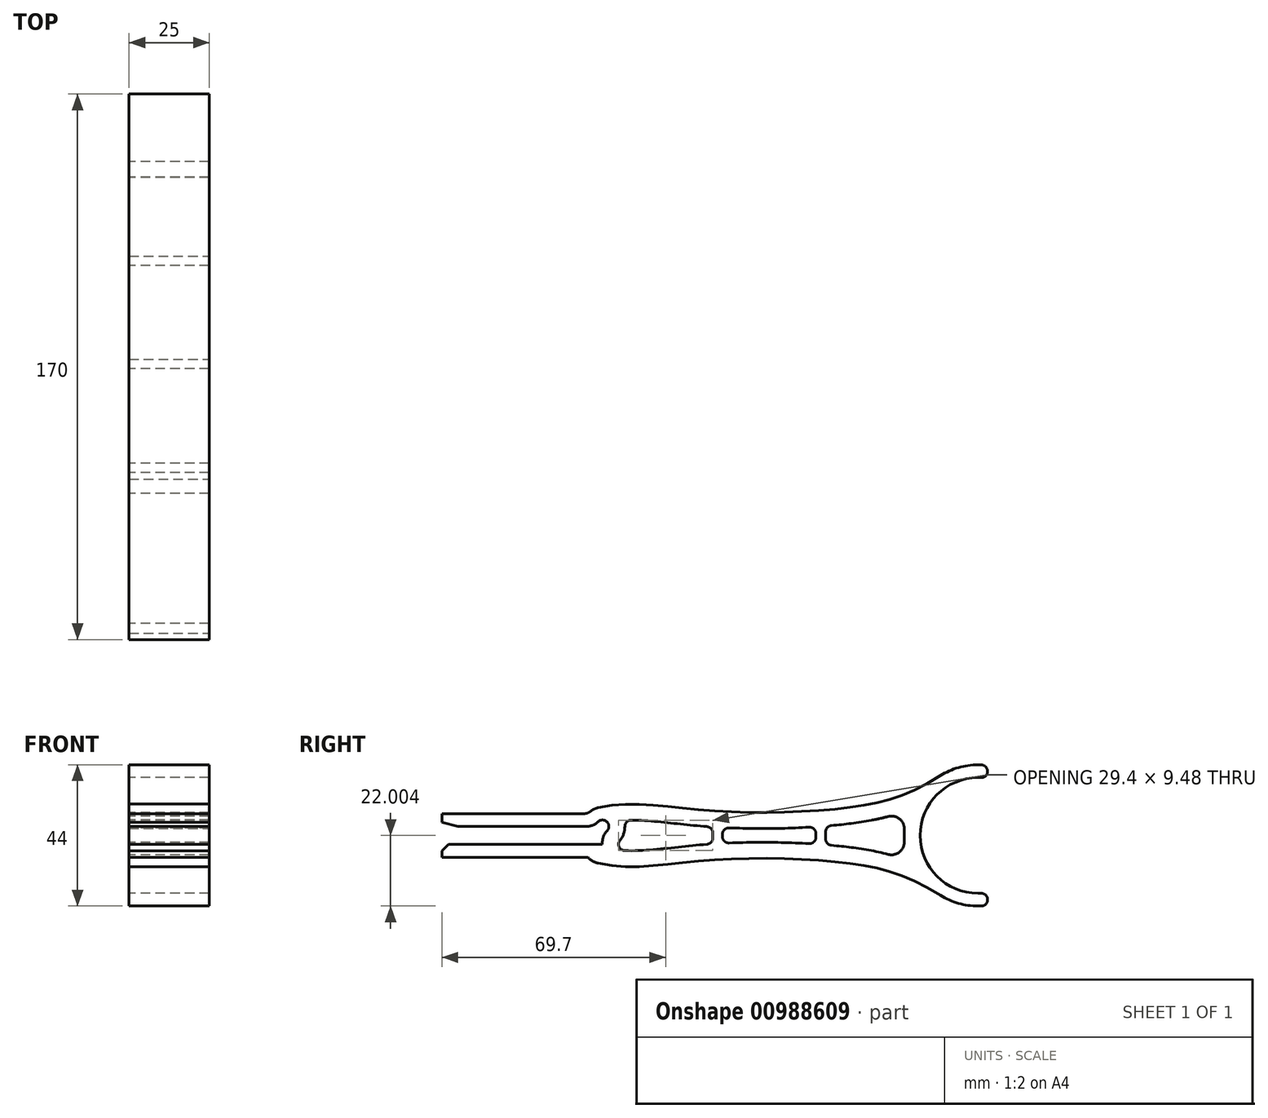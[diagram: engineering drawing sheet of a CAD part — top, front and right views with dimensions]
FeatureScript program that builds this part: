
annotation { "Feature Type Name" : "Feature", "Feature Type Description" : "" }
export const myFeature = defineFeature(function(context is Context, id is Id, definition is map)
    precondition{}
    {
        {
            var Q0;
            Q0=qCreatedBy(makeId("Right.planeOp"),FACE);
            var sketch = newSketch(context, id + "F0", { "sketchPlane" : qUnion([Q0])});
            skLineSegment(sketch, "E0", {"start": v(-50, 0) * mm, "end": v(0, 0) * mm});
            skLineSegment(sketch, "E1", {"start": v(-50, 5.6) * mm, "end": v(-2, 5.6) * mm});
            skArc(sketch, "E2", {"start": v(-2, 5.6) * mm, "mid": v(1.41, 7.01) * mm, "end": v(0, 3.6) * mm});
            skLineSegment(sketch, "E3", {"start": v(0, 3.6) * mm, "end": v(0, 0) * mm});
            skArc(sketch, "E4", {"start": v(-1.34, 11.45) * mm, "mid": v(-3.05, 10.77) * mm, "end": v(-4.47, 9.6) * mm});
            skLineSegment(sketch, "E5", {"start": v(-50, 0) * mm, "end": v(-50, -4) * mm});
            skLineSegment(sketch, "E6", {"start": v(-50, 5.6) * mm, "end": v(-50, 9.6) * mm});
            skLineSegment(sketch, "E7", {"start": v(-50, 9.6) * mm, "end": v(-4.47, 9.6) * mm});
            skLineSegment(sketch, "E8", {"start": v(120, -19.2) * mm, "end": v(120, -15.2) * mm});
            skLineSegment(sketch, "E9", {"start": v(120, -15.2) * mm, "end": v(117, -15.2) * mm});
            skArc(sketch, "E10", {"start": v(117, 20.8) * mm, "mid": v(99, 2.8) * mm, "end": v(117, -15.2) * mm});
            skLineSegment(sketch, "E11", {"start": v(117, 20.8) * mm, "end": v(120, 20.8) * mm});
            skLineSegment(sketch, "E12", {"start": v(120, 20.8) * mm, "end": v(120, 24.8) * mm});
            skLineSegment(sketch, "E13", {"start": v(120, 24.8) * mm, "end": v(117, 24.8) * mm});
            skArc(sketch, "E14", {"start": v(117, 24.8) * mm, "mid": v(110.92, 23.94) * mm, "end": v(105.3, 21.44) * mm});
            skFitSpline(sketch, "E15", {"points": [v(-1.34, 11.45) * mm, v(31.65, 10.65) * mm, v(77.1, 11.53) * mm, v(105.3, 21.44) * mm], "startDerivative": vector(98.91, 22.7) * mm, "endDerivative": vector(98.9, 62.05) * mm});
            skLineSegment(sketch, "E16", {"start": v(-50, 2.8) * mm, "end": v(117, 2.8) * mm, "construction": true});
            skLineSegment(sketch, "E17", {"start": v(-50, 5.6) * mm, "end": v(-50, 0) * mm, "construction": true});
            skLineSegment(sketch, "E18.MirrorCS", {"start": v(-50, -4) * mm, "end": v(-4.47, -4) * mm});
            skArc(sketch, "E19.MirrorCS", {"start": v(-1.34, -5.85) * mm, "mid": v(-3.05, -5.17) * mm, "end": v(-4.47, -4) * mm});
            skArc(sketch, "E20.MirrorCS", {"start": v(117, -19.2) * mm, "mid": v(110.92, -18.34) * mm, "end": v(105.3, -15.84) * mm});
            skLineSegment(sketch, "E21.MirrorCS", {"start": v(120, -19.2) * mm, "end": v(117, -19.2) * mm});
            skFitSpline(sketch, "E22.MirrorCS", {"points": [v(-1.34, -5.85) * mm, v(31.65, -5.05) * mm, v(77.1, -5.93) * mm, v(105.3, -15.84) * mm], "startDerivative": vector(98.91, -22.7) * mm, "endDerivative": vector(98.9, -62.05) * mm});
            skSolve(sketch);
        }
        {
            var Q0;
            Q0 = qSketchRegion(id + "F0", true);
            extrude(context, id + "F1", {"entities" : qUnion([Q0]), "depth" : 25 * mm, "offsetDistance" : 25 * mm});
        }
        {
            var Q0;
            Q0=makeQuery(id+"F1.opExtrude","CAP_FACE",FACE,{"disambiguationData":[OSD([sQuery(id+"F0.wireOp",EDGE,"E0"),sQuery(id+"F0.wireOp",EDGE,"E1"),sQuery(id+"F0.wireOp",EDGE,"E2"),sQuery(id+"F0.wireOp",EDGE,"E3"),sQuery(id+"F0.wireOp",EDGE,"E4"),sQuery(id+"F0.wireOp",EDGE,"E5"),sQuery(id+"F0.wireOp",EDGE,"mtVFrJEV-4ivO-A0F3-py8c-jORwLJyGoYEs"),sQuery(id+"F0.wireOp",EDGE,"E6"),sQuery(id+"F0.wireOp",EDGE,"E7"),sQuery(id+"F0.wireOp",EDGE,"E8"),sQuery(id+"F0.wireOp",EDGE,"E9"),sQuery(id+"F0.wireOp",EDGE,"E10"),sQuery(id+"F0.wireOp",EDGE,"E11"),sQuery(id+"F0.wireOp",EDGE,"E12"),sQuery(id+"F0.wireOp",EDGE,"E13"),sQuery(id+"F0.wireOp",EDGE,"E14"),sQuery(id+"F0.wireOp",EDGE,"E15")])],"isStart":false});
            var Q1;
            Q1=makeQuery(id+"F1.opExtrude","CAP_FACE",FACE,{"disambiguationData":[OSD([sQuery(id+"F0.wireOp",EDGE,"E0"),sQuery(id+"F0.wireOp",EDGE,"E1"),sQuery(id+"F0.wireOp",EDGE,"E2"),sQuery(id+"F0.wireOp",EDGE,"E3"),sQuery(id+"F0.wireOp",EDGE,"E4"),sQuery(id+"F0.wireOp",EDGE,"E5"),sQuery(id+"F0.wireOp",EDGE,"mtVFrJEV-4ivO-A0F3-py8c-jORwLJyGoYEs"),sQuery(id+"F0.wireOp",EDGE,"E6"),sQuery(id+"F0.wireOp",EDGE,"E7"),sQuery(id+"F0.wireOp",EDGE,"E8"),sQuery(id+"F0.wireOp",EDGE,"E9"),sQuery(id+"F0.wireOp",EDGE,"E10"),sQuery(id+"F0.wireOp",EDGE,"E11"),sQuery(id+"F0.wireOp",EDGE,"E12"),sQuery(id+"F0.wireOp",EDGE,"E13"),sQuery(id+"F0.wireOp",EDGE,"E14"),sQuery(id+"F0.wireOp",EDGE,"E15")])],"isStart":true});
            shell(context, id + "F2", {"entities" : qUnion([Q0, Q1]), "thickness" : 5 * mm});
        }
        {
            var Q0;
            Q0=makeQuery(id+"F1.opExtrude","SWEPT_EDGE",EDGE,{"disambiguationData":[OSD([sQuery(id+"F0.wireOp",EDGE,"E8"),sQuery(id+"F0.wireOp",EDGE,"E9")])]});
            var Q1;
            Q1=makeQuery(id+"F1.opExtrude","SWEPT_EDGE",EDGE,{"disambiguationData":[OSD([sQuery(id+"F0.wireOp",EDGE,"E11"),sQuery(id+"F0.wireOp",EDGE,"E12")])]});
            var Q2;
            Q2=makeQuery(id+"F1.opExtrude","SWEPT_EDGE",EDGE,{"disambiguationData":[OSD([sQuery(id+"F0.wireOp",EDGE,"E12"),sQuery(id+"F0.wireOp",EDGE,"E13")])]});
            var Q3;
            Q3=makeQuery(id+"F1.opExtrude","SWEPT_EDGE",EDGE,{"disambiguationData":[OSD([sQuery(id+"F0.wireOp",EDGE,"mtVFrJEV-4ivO-A0F3-py8c-jORwLJyGoYEs"),sQuery(id+"F0.wireOp",EDGE,"E8")])]});
            fillet(context, id + "F3", {"entities" : qUnion([Q0, Q1, Q2, Q3]), "radius" : 2 * mm, "tangentPropagation" : true, "allowEdgeOverflow" : false});
        }
        {
            var Q0;
            Q0=makeQuery(id+"F1.opExtrude","SWEPT_EDGE",EDGE,{"disambiguationData":[OSD([sQuery(id+"F0.wireOp",EDGE,"E2"),sQuery(id+"F0.wireOp",EDGE,"E3")])]});
            var Q1;
            Q1=makeQuery(id+"F1.opExtrude","SWEPT_EDGE",EDGE,{"disambiguationData":[OSD([sQuery(id+"F0.wireOp",EDGE,"E1"),sQuery(id+"F0.wireOp",EDGE,"E2")])]});
            fillet(context, id + "F4", {"entities" : qUnion([Q0, Q1]), "radius" : 5 * mm, "tangentPropagation" : true, "allowEdgeOverflow" : false});
        }
        {
            var Q0;
            Q0=makeQuery(id+"F1.opExtrude","SWEPT_EDGE",EDGE,{"disambiguationData":[OSD([sQuery(id+"F0.wireOp",EDGE,"E4"),sQuery(id+"F0.wireOp",EDGE,"E7")])]});
            fillet(context, id + "F5", {"entities" : qUnion([Q0]), "radius" : 3 * mm, "tangentPropagation" : true, "allowEdgeOverflow" : false});
        }
        {
            var Q0;
            Q0=makeQuery(id+"F1.opExtrude","SWEPT_EDGE",EDGE,{"disambiguationData":[OSD([sQuery(id+"F0.wireOp",EDGE,"E1"),sQuery(id+"F0.wireOp",EDGE,"E6")])]});
            chamfer(context, id + "F6", {"entities" : qUnion([Q0]), "chamferType" : ChamferType.OFFSET_ANGLE, "width" : 5 * mm, "oppositeDirection" : false, "angle" : 15 * degree, "tangentPropagation" : true});
        }
        {
            var Q0;
            Q0=makeQuery(id+"F1.opExtrude","SWEPT_EDGE",EDGE,{"disambiguationData":[OSD([sQuery(id+"F0.wireOp",EDGE,"E0"),sQuery(id+"F0.wireOp",EDGE,"E5")])]});
            chamfer(context, id + "F7", {"entities" : qUnion([Q0]), "width" : 2 * mm, "tangentPropagation" : true});
        }
        {
            var Q0;
            Q0=makeQuery(id+"F1.opExtrude","CAP_FACE",FACE,{"disambiguationData":[OSD([sQuery(id+"F0.wireOp",EDGE,"E0"),sQuery(id+"F0.wireOp",EDGE,"E1"),sQuery(id+"F0.wireOp",EDGE,"E2"),sQuery(id+"F0.wireOp",EDGE,"E3"),sQuery(id+"F0.wireOp",EDGE,"E4"),sQuery(id+"F0.wireOp",EDGE,"E5"),sQuery(id+"F0.wireOp",EDGE,"mtVFrJEV-4ivO-A0F3-py8c-jORwLJyGoYEs"),sQuery(id+"F0.wireOp",EDGE,"E6"),sQuery(id+"F0.wireOp",EDGE,"E7"),sQuery(id+"F0.wireOp",EDGE,"E8"),sQuery(id+"F0.wireOp",EDGE,"E9"),sQuery(id+"F0.wireOp",EDGE,"E10"),sQuery(id+"F0.wireOp",EDGE,"E11"),sQuery(id+"F0.wireOp",EDGE,"E12"),sQuery(id+"F0.wireOp",EDGE,"E13"),sQuery(id+"F0.wireOp",EDGE,"E14"),sQuery(id+"F0.wireOp",EDGE,"E15")])],"isStart":true});
            var sketch = newSketch(context, id + "F8", { "sketchPlane" : qUnion([Q0])});
            skLineSegment(sketch, "E23.bottom", {"start": v(-69.53, -4.91) * mm, "end": v(-66.53, -4.91) * mm});
            skLineSegment(sketch, "E23.top", {"start": v(-69.53, 10.51) * mm, "end": v(-66.53, 10.51) * mm});
            skLineSegment(sketch, "E23.left", {"start": v(-69.53, -4.91) * mm, "end": v(-69.53, 10.51) * mm});
            skLineSegment(sketch, "E23.right", {"start": v(-66.53, -4.91) * mm, "end": v(-66.53, 10.51) * mm});
            skLineSegment(sketch, "E24.bottom", {"start": v(-34.4, -4.66) * mm, "end": v(-37.4, -4.66) * mm});
            skLineSegment(sketch, "E24.top", {"start": v(-34.4, 10.26) * mm, "end": v(-37.4, 10.26) * mm});
            skLineSegment(sketch, "E24.left", {"start": v(-34.4, -4.66) * mm, "end": v(-34.4, 10.26) * mm});
            skLineSegment(sketch, "E24.right", {"start": v(-37.4, -4.66) * mm, "end": v(-37.4, 10.26) * mm});
            skSolve(sketch);
        }
        {
            var Q0;
            Q0 = qSketchRegion(id + "F8", true);
            var Q1;
            Q1=makeQuery(id+"F1.opExtrude","CAP_FACE",FACE,{"disambiguationData":[OSD([sQuery(id+"F0.wireOp",EDGE,"E0"),sQuery(id+"F0.wireOp",EDGE,"E1"),sQuery(id+"F0.wireOp",EDGE,"E2"),sQuery(id+"F0.wireOp",EDGE,"E3"),sQuery(id+"F0.wireOp",EDGE,"E4"),sQuery(id+"F0.wireOp",EDGE,"E5"),sQuery(id+"F0.wireOp",EDGE,"mtVFrJEV-4ivO-A0F3-py8c-jORwLJyGoYEs"),sQuery(id+"F0.wireOp",EDGE,"E6"),sQuery(id+"F0.wireOp",EDGE,"E7"),sQuery(id+"F0.wireOp",EDGE,"E8"),sQuery(id+"F0.wireOp",EDGE,"E9"),sQuery(id+"F0.wireOp",EDGE,"E10"),sQuery(id+"F0.wireOp",EDGE,"E11"),sQuery(id+"F0.wireOp",EDGE,"E12"),sQuery(id+"F0.wireOp",EDGE,"E13"),sQuery(id+"F0.wireOp",EDGE,"E14"),sQuery(id+"F0.wireOp",EDGE,"E15")])],"isStart":false});
            extrude(context, id + "F9", {"entities" : qUnion([Q0]), "operationType" : NewBodyOperationType.ADD, "endBound" : BoundingType.UP_TO_SURFACE, "oppositeDirection" : true, "depth" : 25 * mm, "endBoundEntityFace" : qUnion([Q1]), "offsetDistance" : 25 * mm});
        }
        {
            var Q0;
            Q0=makeQuery(id+"F2.opShell","TWEAK_EDGE",EDGE,{"derivedFrom":[makeQuery(id+"F1.opExtrude","SWEPT_FACE",FACE,{"disambiguationData":[OSD([sQuery(id+"F0.wireOp",EDGE,"E10")])]}),makeQuery(id+"F1.opExtrude","SWEPT_FACE",FACE,{"disambiguationData":[OSD([sQuery(id+"F0.wireOp",EDGE,"E15")])]})]});
            var Q1;
            Q1=makeQuery(id+"F2.opShell","TWEAK_EDGE",EDGE,{"derivedFrom":[makeQuery(id+"F1.opExtrude","SWEPT_FACE",FACE,{"disambiguationData":[OSD([sQuery(id+"F0.wireOp",EDGE,"mtVFrJEV-4ivO-A0F3-py8c-jORwLJyGoYEs")])]}),makeQuery(id+"F1.opExtrude","SWEPT_FACE",FACE,{"disambiguationData":[OSD([sQuery(id+"F0.wireOp",EDGE,"E10")])]})]});
            var Q2;
            Q2=makeQuery(id+"F2.opShell","TWEAK_EDGE",EDGE,{"derivedFrom":[makeQuery(id+"F1.opExtrude","SWEPT_FACE",FACE,{"disambiguationData":[OSD([sQuery(id+"F0.wireOp",EDGE,"E10")])]}),makeQuery(id+"F1.opExtrude","SWEPT_FACE",FACE,{"disambiguationData":[OSD([sQuery(id+"F0.wireOp",EDGE,"E22.MirrorCS")])]})]});
            fillet(context, id + "F10", {"entities" : qUnion([Q0, Q1, Q2]), "radius" : 4 * mm, "tangentPropagation" : true, "allowEdgeOverflow" : false});
        }
        {
            var Q0;
            Q0=makeQuery(id+"F2.opShell","TWEAK_EDGE",EDGE,{"derivedFrom":[makeQuery(id+"F1.opExtrude","SWEPT_FACE",FACE,{"disambiguationData":[OSD([sQuery(id+"F0.wireOp",EDGE,"E2")])]}),makeQuery(id+"F1.opExtrude","SWEPT_FACE",FACE,{"disambiguationData":[OSD([sQuery(id+"F0.wireOp",EDGE,"E15")])]})]});
            var Q1;
            Q1=makeQuery(id+"F2.opShell","TWEAK_EDGE",EDGE,{"derivedFrom":[makeQuery(id+"F1.opExtrude","SWEPT_FACE",FACE,{"disambiguationData":[OSD([sQuery(id+"F0.wireOp",EDGE,"E2")])]}),makeQuery(id+"F1.opExtrude","SWEPT_FACE",FACE,{"disambiguationData":[OSD([sQuery(id+"F0.wireOp",EDGE,"mtVFrJEV-4ivO-A0F3-py8c-jORwLJyGoYEs")])]})]});
            var Q2;
            Q2=makeQuery(id+"F2.opShell","TWEAK_EDGE",EDGE,{"derivedFrom":[makeQuery(id+"F1.opExtrude","SWEPT_FACE",FACE,{"disambiguationData":[OSD([sQuery(id+"F0.wireOp",EDGE,"E3")])]}),makeQuery(id+"F1.opExtrude","SWEPT_FACE",FACE,{"disambiguationData":[OSD([sQuery(id+"F0.wireOp",EDGE,"E22.MirrorCS")])]})]});
            var Q3;
            Q3=makeQuery(id+"F2.opShell","OFFSET_EDGE",EDGE,{"disambiguationData":[OSD([sQuery(id+"F0.wireOp",EDGE,"E2"),sQuery(id+"F0.wireOp",EDGE,"E3")])]});
            fillet(context, id + "F11", {"entities" : qUnion([Q0, Q1, Q2, Q3]), "radius" : 2 * mm, "tangentPropagation" : true, "allowEdgeOverflow" : false});
        }
        {
            var Q0;
            Q0=makeQuery(id+"F9.boolean.opBoolean","INTERSECT",EDGE,{"derivedFrom":[makeQuery(id+"F2.opShell","OFFSET_FACE",FACE,{"disambiguationData":[OSD([sQuery(id+"F0.wireOp",EDGE,"E22.MirrorCS")])]}),makeQuery(id+"F9.opExtrude","SWEPT_FACE",FACE,{"disambiguationData":[OSD([sQuery(id+"F8.wireOp",EDGE,"E23.left")])]})]});
            var Q1;
            Q1=makeQuery(id+"F9.boolean.opBoolean","INTERSECT",EDGE,{"derivedFrom":[makeQuery(id+"F2.opShell","OFFSET_FACE",FACE,{"disambiguationData":[OSD([sQuery(id+"F0.wireOp",EDGE,"E22.MirrorCS")])]}),makeQuery(id+"F9.opExtrude","SWEPT_FACE",FACE,{"disambiguationData":[OSD([sQuery(id+"F8.wireOp",EDGE,"E24.right")])]})]});
            var Q2;
            Q2=makeQuery(id+"F9.boolean.opBoolean","INTERSECT",EDGE,{"derivedFrom":[makeQuery(id+"F2.opShell","OFFSET_FACE",FACE,{"disambiguationData":[OSD([sQuery(id+"F0.wireOp",EDGE,"E15")])]}),makeQuery(id+"F9.opExtrude","SWEPT_FACE",FACE,{"disambiguationData":[OSD([sQuery(id+"F8.wireOp",EDGE,"E23.left")])]})]});
            var Q3;
            Q3=makeQuery(id+"F9.boolean.opBoolean","INTERSECT",EDGE,{"derivedFrom":[makeQuery(id+"F2.opShell","OFFSET_FACE",FACE,{"disambiguationData":[OSD([sQuery(id+"F0.wireOp",EDGE,"E22.MirrorCS")])]}),makeQuery(id+"F9.opExtrude","SWEPT_FACE",FACE,{"disambiguationData":[OSD([sQuery(id+"F8.wireOp",EDGE,"E23.right")])]})]});
            var Q4;
            Q4=makeQuery(id+"F9.boolean.opBoolean","INTERSECT",EDGE,{"derivedFrom":[makeQuery(id+"F2.opShell","OFFSET_FACE",FACE,{"disambiguationData":[OSD([sQuery(id+"F0.wireOp",EDGE,"E22.MirrorCS")])]}),makeQuery(id+"F9.opExtrude","SWEPT_FACE",FACE,{"disambiguationData":[OSD([sQuery(id+"F8.wireOp",EDGE,"E24.left")])]})]});
            var Q5;
            Q5=makeQuery(id+"F9.boolean.opBoolean","INTERSECT",EDGE,{"derivedFrom":[makeQuery(id+"F2.opShell","OFFSET_FACE",FACE,{"disambiguationData":[OSD([sQuery(id+"F0.wireOp",EDGE,"E15")])]}),makeQuery(id+"F9.opExtrude","SWEPT_FACE",FACE,{"disambiguationData":[OSD([sQuery(id+"F8.wireOp",EDGE,"E23.right")])]})]});
            var Q6;
            Q6=makeQuery(id+"F9.boolean.opBoolean","INTERSECT",EDGE,{"derivedFrom":[makeQuery(id+"F2.opShell","OFFSET_FACE",FACE,{"disambiguationData":[OSD([sQuery(id+"F0.wireOp",EDGE,"E15")])]}),makeQuery(id+"F9.opExtrude","SWEPT_FACE",FACE,{"disambiguationData":[OSD([sQuery(id+"F8.wireOp",EDGE,"E24.left")])]})]});
            var Q7;
            Q7=makeQuery(id+"F9.boolean.opBoolean","INTERSECT",EDGE,{"derivedFrom":[makeQuery(id+"F2.opShell","OFFSET_FACE",FACE,{"disambiguationData":[OSD([sQuery(id+"F0.wireOp",EDGE,"E15")])]}),makeQuery(id+"F9.opExtrude","SWEPT_FACE",FACE,{"disambiguationData":[OSD([sQuery(id+"F8.wireOp",EDGE,"E24.right")])]})]});
            fillet(context, id + "F12", {"entities" : qUnion([Q0, Q1, Q2, Q3, Q4, Q5, Q6, Q7]), "radius" : 2 * mm, "tangentPropagation" : true, "allowEdgeOverflow" : false});
        }
    });
